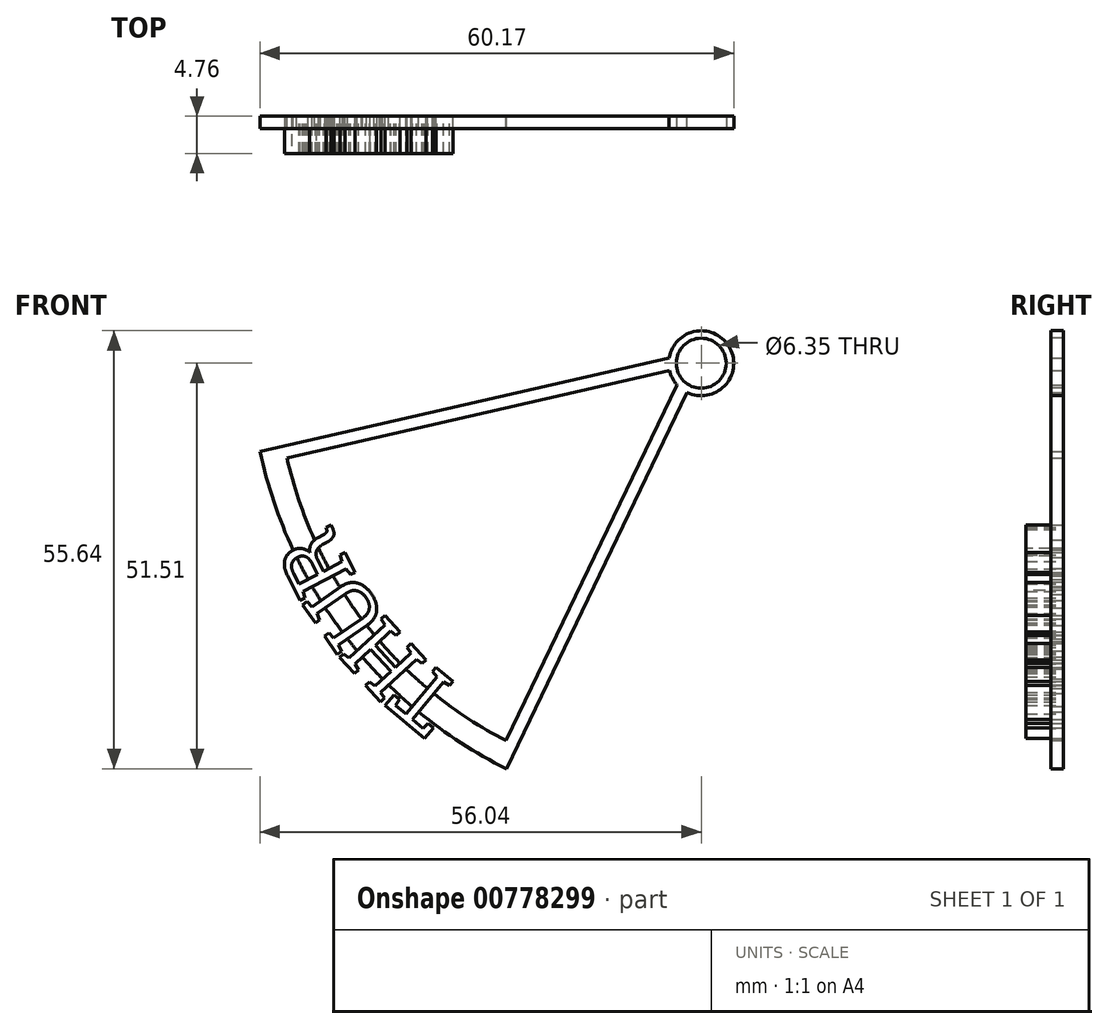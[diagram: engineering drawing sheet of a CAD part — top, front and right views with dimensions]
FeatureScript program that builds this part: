
annotation { "Feature Type Name" : "Feature", "Feature Type Description" : "" }
export const myFeature = defineFeature(function(context is Context, id is Id, definition is map)
    precondition{}
    {
        {
            var Q0;
            Q0=qCreatedBy(makeId("Front.planeOp"),FACE);
            var sketch = newSketch(context, id + "F0", { "sketchPlane" : qUnion([Q0])});
            skCircle(sketch, "E0", {"center": v(0, 0) * mm, "radius": 59.18 * mm, "construction": true});
            skCircle(sketch, "E1", {"center": v(0, 0) * mm, "radius": 50.8 * mm, "construction": true});
            skLineSegment(sketch, "E2", {"start": v(0, 0) * mm, "end": v(0, 59.18) * mm, "construction": true});
            skLineSegment(sketch, "E3", {"start": v(0, 0) * mm, "end": v(-25.65, -53.34) * mm, "construction": true});
            skLineSegment(sketch, "E4", {"start": v(0, 0) * mm, "end": v(-37.88, -45.47) * mm, "construction": true});
            skLineSegment(sketch, "E5", {"start": v(0, 0) * mm, "end": v(-43.5, -40.14) * mm, "construction": true});
            skLineSegment(sketch, "E6", {"start": v(0, 0) * mm, "end": v(-52.64, -27.05) * mm, "construction": true});
            skText(sketch, "E7", { "text": "T", "fontName": "RobotoSlab-Regular.ttf"});
            skText(sketch, "E8", { "text": "H", "fontName": "RobotoSlab-Regular.ttf"});
            skText(sketch, "E9", { "text": "R", "fontName": "RobotoSlab-Regular.ttf"});
            skLineSegment(sketch, "E10", {"start": v(0, 0) * mm, "end": v(-35.04, -47.84) * mm, "construction": true});
            skLineSegment(sketch, "E11", {"start": v(0, 0) * mm, "end": v(-54.42, -23.6) * mm, "construction": true});
            skLineSegment(sketch, "E12", {"start": v(0, 0) * mm, "end": v(-57.69, -13.21) * mm, "construction": true});
            skText(sketch, "E13", { "text": "U", "fontName": "RobotoSlab-Regular.ttf"});
            skLineSegment(sketch, "E14", {"start": v(0, 0) * mm, "end": v(-48.63, -33.73) * mm, "construction": true});
            const initialGuessF0  = {"E7": [-0.02996, -0.04174, -0.76832, 0.64007, 0.00794], "E8": [-0.0347, -0.03797, -0.6782, 0.73488, 0.00794], "E9": [-0.0438, -0.02689, -0.45715, 0.8894, 0.00794], "E13": [-0.03962, -0.03277, -0.57, 0.82165, 0.00795]};
            skSetInitialGuess(sketch, initialGuessF0);
            skSolve(sketch);
        }
        {
            var Q0;
            Q0=qSketchRegion(id+"F0",true);
            extrude(context, id + "F1", {"entities" : qUnion([Q0]), "depth" : 4.76 * mm, "offsetDistance" : 25.4 * mm});
        }
        {
            var Q0;
            Q0=qCreatedBy(makeId("Front.planeOp"),FACE);
            var sketch = newSketch(context, id + "F2", { "sketchPlane" : qUnion([Q0])});
            skCircle(sketch, "E15", {"center": v(0, 0) * mm, "radius": 57.15 * mm, "construction": true});
            skCircle(sketch, "E16", {"center": v(0, 0) * mm, "radius": 53.98 * mm, "construction": true});
            skCircle(sketch, "E17", {"center": v(0, 0) * mm, "radius": 4.13 * mm, "construction": true});
            skLineSegment(sketch, "E18", {"start": v(0, 0) * mm, "end": v(0, 57.15) * mm, "construction": true});
            skLineSegment(sketch, "E19", {"start": v(0, 0) * mm, "end": v(-24.77, -51.5) * mm, "construction": true});
            skLineSegment(sketch, "E20", {"start": v(0, 0) * mm, "end": v(-52.61, -12.05) * mm, "construction": true});
            skLineSegment(sketch, "E21", {"start": v(-24.81, -47.93) * mm, "end": v(-3.08, -2.75) * mm, "construction": true});
            skLineSegment(sketch, "E22", {"start": v(-56.04, -11.2) * mm, "end": v(-4.07, 0.7) * mm, "construction": true});
            skLineSegment(sketch, "E23", {"start": v(-52.61, -12.05) * mm, "end": v(-4.02, -0.92) * mm});
            skLineSegment(sketch, "E24", {"start": v(-24.81, -47.93) * mm, "end": v(-3.08, -2.75) * mm});
            skLineSegment(sketch, "E25", {"start": v(-24.77, -51.5) * mm, "end": v(-1.79, -3.72) * mm});
            skLineSegment(sketch, "E26", {"start": v(-56.04, -11.2) * mm, "end": v(-4.07, 0.7) * mm});
            skCircle(sketch, "E27", {"center": v(0, 0) * mm, "radius": 4.13 * mm});
            skArc(sketch, "E28", {"start": v(-52.61, -12.05) * mm, "mid": v(-42.69, -33.07) * mm, "end": v(-24.81, -47.93) * mm});
            skArc(sketch, "E29", {"start": v(-56.04, -11.2) * mm, "mid": v(-45, -34.92) * mm, "end": v(-24.77, -51.5) * mm});
            skSolve(sketch);
        }
        {
            var Q0;
            {var subQ3=sQuery(id+"F2.wireOp",EDGE,"E23");Q0=makeQuery(id+"F2.imprint","IMPRINT",FACE,{"disambiguationData":[TD([[makeQuery(id+"F2.imprint","IMPRINT",EDGE,{"derivedFrom":subQ3}),1.0]])]});}
            var Q1;
            {var subQ0=sQuery(id+"F2.wireOp",EDGE,"E27");var subQ1=makeQuery(id+"F2.imprint","INTERSECT",VERTEX,{"derivedFrom":[sQuery(id+"F2.wireOp",EDGE,"E23"),subQ0]});Q1=makeQuery(id+"F2.imprint","IMPRINT",FACE,{"disambiguationData":[TD([[makeQuery(id+"F2.imprint","IMPRINT",EDGE,{"disambiguationData":[TD([[subQ1,1.0]])],"derivedFrom":subQ0}),1.0]])]});}
            extrude(context, id + "F3", {"entities" : qUnion([Q0, Q1]), "operationType" : NewBodyOperationType.ADD, "depth" : 1.59 * mm, "offsetDistance" : 25.4 * mm});
        }
        {
            var Q0;
            {var subQ0=sQuery(id+"F2.wireOp",EDGE,"E26");var subQ1=sQuery(id+"F2.wireOp",EDGE,"E25");var subQ2=sQuery(id+"F2.wireOp",EDGE,"E24");var subQ3=sQuery(id+"F2.wireOp",EDGE,"E23");var subQ4=sQuery(id+"F2.wireOp",EDGE,"E28");var subQ5=sQuery(id+"F2.wireOp",EDGE,"E27");var subQ6=sQuery(id+"F2.wireOp",EDGE,"E29");Q0=makeQuery(id+"F3.boolean.opBoolean","SPLIT",FACE,{"disambiguationData":[TD([makeQuery(id+"F1.opExtrude","SWEPT_FACE",FACE,{"disambiguationData":[OSD([sQuery(id+"F0.wireOp",EDGE,"E7.sketch_text.stroke-10")])]})])],"derivedFrom":makeQuery(id+"F3.opExtrude","CAP_FACE",FACE,{"disambiguationData":[OSD([subQ3,subQ2,subQ1,subQ0,subQ5,subQ4,subQ6])],"isStart":false})});}
            var sketch = newSketch(context, id + "F4", { "sketchPlane" : qUnion([Q0])});
            skPoint(sketch, "E30", {"position": v(0, 0) * mm});
            skSolve(sketch);
        }
        {
            var Q0;
            Q0=sQuery(id+"F4.wireOp",VERTEX,"E30");
            var Q1;
            Q1=makeQuery(id+"F1.opExtrude","SWEPT_BODY",BODY,{"disambiguationData":[OSD([sQuery(id+"F0.wireOp",EDGE,"E7.sketch_text.stroke-0"),sQuery(id+"F0.wireOp",EDGE,"E7.sketch_text.stroke-1"),sQuery(id+"F0.wireOp",EDGE,"E7.sketch_text.stroke-2"),sQuery(id+"F0.wireOp",EDGE,"E7.sketch_text.stroke-3"),sQuery(id+"F0.wireOp",EDGE,"E7.sketch_text.stroke-4"),sQuery(id+"F0.wireOp",EDGE,"E7.sketch_text.stroke-5"),sQuery(id+"F0.wireOp",EDGE,"E7.sketch_text.stroke-6"),sQuery(id+"F0.wireOp",EDGE,"E7.sketch_text.stroke-7"),sQuery(id+"F0.wireOp",EDGE,"E7.sketch_text.stroke-8"),sQuery(id+"F0.wireOp",EDGE,"E7.sketch_text.stroke-9"),sQuery(id+"F0.wireOp",EDGE,"E7.sketch_text.stroke-10"),sQuery(id+"F0.wireOp",EDGE,"E7.sketch_text.stroke-11"),sQuery(id+"F0.wireOp",EDGE,"E7.sketch_text.stroke-12"),sQuery(id+"F0.wireOp",EDGE,"E7.sketch_text.stroke-13"),sQuery(id+"F0.wireOp",EDGE,"E7.sketch_text.stroke-14"),sQuery(id+"F0.wireOp",EDGE,"E7.sketch_text.stroke-15")])]});
            hole(context, id + "F5", {"style" : HoleStyle.SIMPLE, "endStyle" : HoleEndStyle.THROUGH, "holeDiameter" : 6.35 * mm, "majorDiameter" : 6.35 * mm, "isTappedThrough" : true, "tappedDepth" : 12.7 * mm, "tapClearance" : 3, "locations" : qUnion([Q0]), "scope" : qUnion([Q1])});
        }
    });
